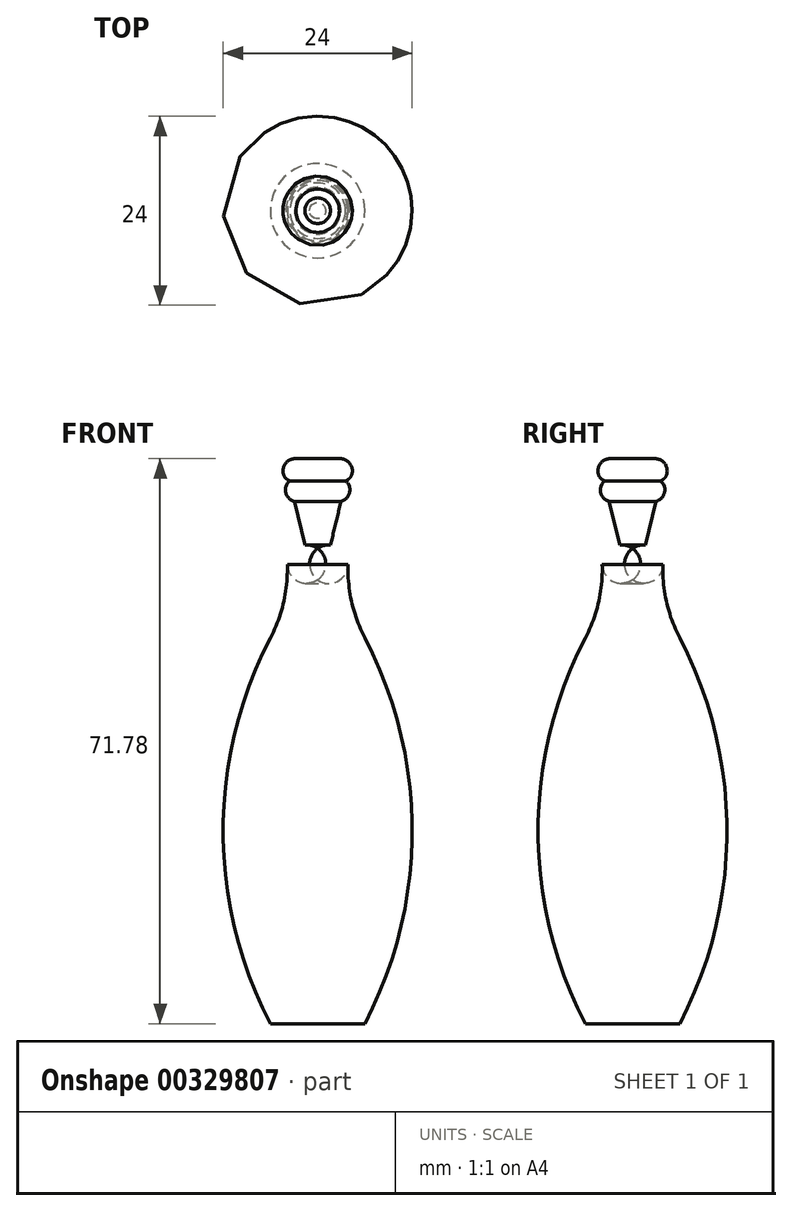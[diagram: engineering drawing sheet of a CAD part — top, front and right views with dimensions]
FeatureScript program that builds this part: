
annotation { "Feature Type Name" : "Feature", "Feature Type Description" : "" }
export const myFeature = defineFeature(function(context is Context, id is Id, definition is map)
    precondition{}
    {
        {
            var Q0;
            Q0=qCreatedBy(makeId("Front.planeOp"),FACE);
            var sketch = newSketch(context, id + "F0", { "sketchPlane" : qUnion([Q0])});
            skLineSegment(sketch, "E0", {"start": v(0, -75) * mm, "end": v(6, -75) * mm});
            skLineSegment(sketch, "E1", {"start": v(0, 0) * mm, "end": v(0, -75) * mm});
            skArc(sketch, "E2", {"start": v(6, -75) * mm, "mid": v(12, -50.5) * mm, "end": v(6, -26.01) * mm});
            skArc(sketch, "E3", {"start": v(3.86, -16.7) * mm, "mid": v(4.33, -21.49) * mm, "end": v(6, -26.01) * mm});
            skArc(sketch, "E4", {"start": v(3.86, -16.7) * mm, "mid": v(3.24, -15) * mm, "end": v(1.63, -14.19) * mm});
            skLineSegment(sketch, "E5", {"start": v(1.63, -14.19) * mm, "end": v(2.97, -8.64) * mm});
            skArc(sketch, "E6", {"start": v(2.97, -8.64) * mm, "mid": v(4.06, -7.51) * mm, "end": v(3.53, -6.03) * mm});
            skArc(sketch, "E7", {"start": v(3.53, -6.03) * mm, "mid": v(4.01, -5.76) * mm, "end": v(4.32, -5.28) * mm});
            skArc(sketch, "E8", {"start": v(4.32, -5.28) * mm, "mid": v(4.09, -3.84) * mm, "end": v(2.76, -3.22) * mm});
            skArc(sketch, "E9", {"start": v(0, 0) * mm, "mid": v(0.78, -2.12) * mm, "end": v(2.76, -3.22) * mm});
            skSolve(sketch);
        }
        {
            var Q0;
            Q0=makeQuery(id+"F0.imprint","IMPRINT",FACE,{"disambiguationData":[TD([[makeQuery(id+"F0.imprint","IMPRINT",EDGE,{"derivedFrom":sQuery(id+"F0.wireOp",EDGE,"E0")}),1.0]])]});
            var Q1;
            Q1=sQuery(id+"F0.wireOp",EDGE,"E1");
            revolve(context, id + "F1", {"entities" : qUnion([Q0]), "axis" : qUnion([Q1]), "revolveType" : RevolveType.FULL});
        }
    });
